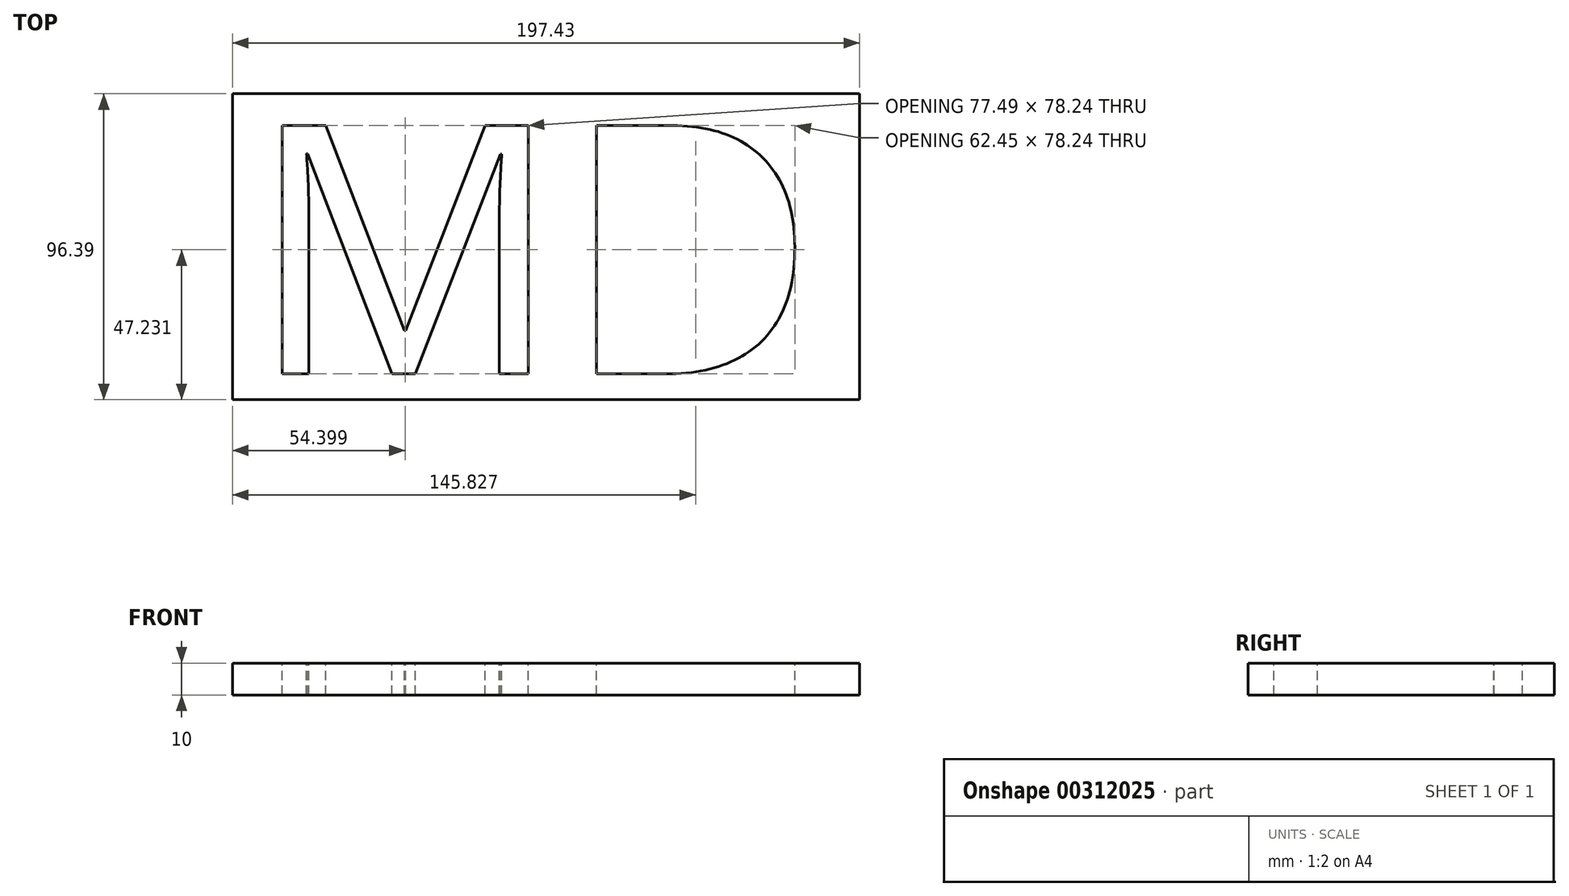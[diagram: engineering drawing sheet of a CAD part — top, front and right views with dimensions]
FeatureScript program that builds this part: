
annotation { "Feature Type Name" : "Feature", "Feature Type Description" : "" }
export const myFeature = defineFeature(function(context is Context, id is Id, definition is map)
    precondition{}
    {
        {
            var Q0;
            Q0=qCreatedBy(makeId("Top.planeOp"),FACE);
            var sketch = newSketch(context, id + "F0", { "sketchPlane" : qUnion([Q0])});
            skLineSegment(sketch, "E0.bottom", {"start": v(-125.6, 35.34) * mm, "end": v(71.83, 35.34) * mm});
            skLineSegment(sketch, "E0.top", {"start": v(-125.6, -61.05) * mm, "end": v(71.83, -61.05) * mm});
            skLineSegment(sketch, "E0.left", {"start": v(-125.6, 35.34) * mm, "end": v(-125.6, -61.05) * mm});
            skLineSegment(sketch, "E0.right", {"start": v(71.83, 35.34) * mm, "end": v(71.83, -61.05) * mm});
            skText(sketch, "E1", { "text": "MD\n", "fontName": "OpenSans-Regular.ttf"});
            const initialGuessF0  = {"E1": [-0.1207, -0.05294, 1, 0, 0.07891]};
            skSetInitialGuess(sketch, initialGuessF0);
            skSolve(sketch);
        }
        {
            var Q0;
            Q0 = qSketchRegion(id + "F0", true);
            extrude(context, id + "F1", {"entities" : qUnion([Q0]), "oppositeDirection" : true, "depth" : 8 * mm});
        }
        {
            var Q0;
            Q0 = qSketchRegion(id + "F0", true);
            extrude(context, id + "F2", {"entities" : qUnion([Q0]), "operationType" : NewBodyOperationType.ADD, "depth" : 2 * mm});
        }
    });
